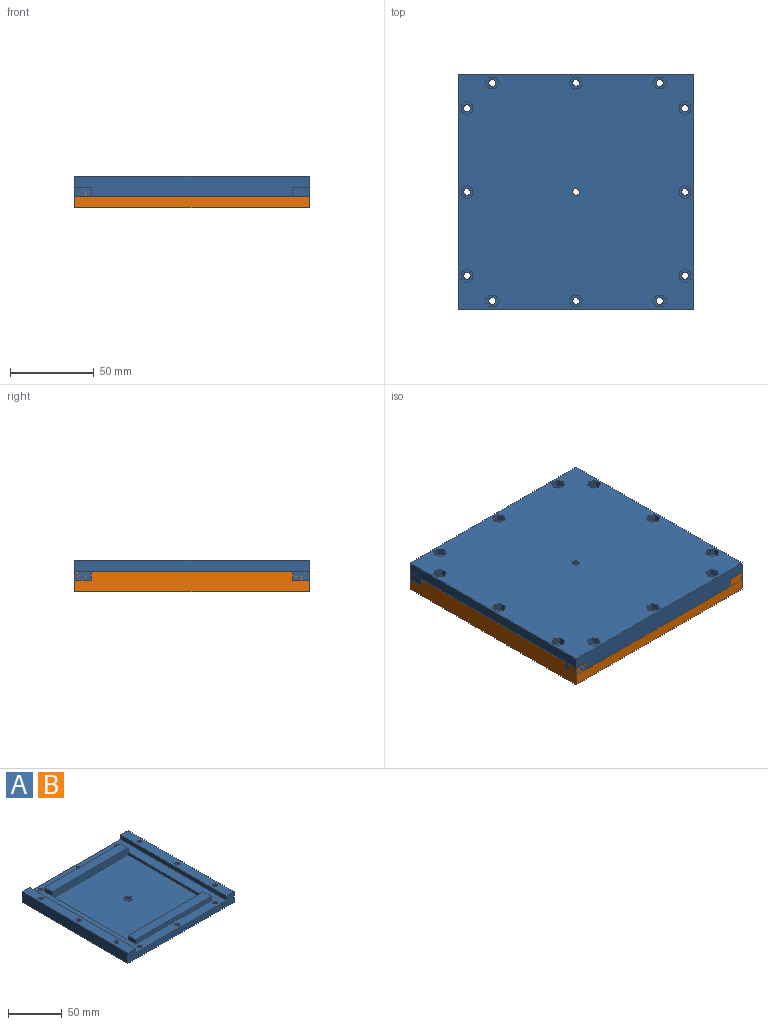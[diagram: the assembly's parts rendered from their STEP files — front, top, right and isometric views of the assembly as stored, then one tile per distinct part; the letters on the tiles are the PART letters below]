
ASSEMBLY  parts=2 mates=1
PART A: 127 faces, bbox 140x140x12 mm
  f0: plane 140x140mm, normal (0,0,-1), area 19062.3mm2, adj f15,f16,f17,f18,f42,f43,f44,f45
  f1: cylinder r=2.1mm len=8mm, axis (0,0,1), area 105.6mm2, adj f34,f126
  f2: cylinder r=2.1mm len=8mm, axis (0,0,1), area 105.6mm2, adj f34,f119
  f3: cylinder r=2.1mm len=8mm, axis (0,0,1), area 105.6mm2, adj f34,f112
  f4: cylinder r=2.1mm len=8mm, axis (0,0,1), area 105.6mm2, adj f32,f105
  f5: cylinder r=2.1mm len=8mm, axis (0,0,1), area 105.6mm2, adj f32,f98
  f6: cylinder r=2.1mm len=8mm, axis (0,0,1), area 105.6mm2, adj f32,f91
  f7: cylinder r=2.1mm len=4.2mm, axis (0,0,1), area 39.6mm2, adj f14,f84
  f8: cylinder r=2.1mm len=4.2mm, axis (0,0,1), area 39.6mm2, adj f14,f77
  f9: cylinder r=2.1mm len=4.2mm, axis (0,0,1), area 39.6mm2, adj f14,f70
  f10: cylinder r=2.1mm len=4.2mm, axis (0,0,1), area 39.6mm2, adj f14,f63
  f11: cylinder r=2.1mm len=4.2mm, axis (0,0,1), area 39.6mm2, adj f14,f56
  f12: cylinder r=2.1mm len=4.2mm, axis (0,0,1), area 39.6mm2, adj f14,f49
  f13: plane 100x100mm, normal (0,0,1), area 9956.3mm2, adj f19,f20,f21,f22,f35,f36,f37,f38
  f14: plane 140x120mm, normal (0,0,1), area 4716.9mm2, adj f7,f8,f9,f10,f11,f12,f16,f18
  f15: plane 140x12mm, normal (1,0,0), area 1680mm2, adj f0,f16,f18,f32
  f16: plane 140x12mm, normal (0,1,0), area 1080mm2, adj f0,f14,f15,f17,f31,f32,f33,f34
  f17: plane 140x12mm, normal (-1,0,0), area 1680mm2, adj f0,f16,f18,f34
  f18: plane 140x12mm, normal (0,-1,0), area 1080mm2, adj f0,f14,f15,f17,f31,f32,f33,f34
  f19: plane 100x8mm, normal (0,-1,0), area 800mm2, adj f13,f20,f22,f23,f24,f26
  f20: plane 100x3mm, normal (-1,0,0), area 300mm2, adj f13,f14,f19,f21
  f21: plane 100x8mm, normal (0,1,0), area 800mm2, adj f13,f20,f22,f27,f29,f30
  f22: plane 100x3mm, normal (1,0,0), area 300mm2, adj f13,f14,f19,f21
  f23: plane 10x5mm, normal (-1,0,0), area 50mm2, adj f14,f19,f25,f26
  f24: plane 10x5mm, normal (1,0,0), area 50mm2, adj f14,f19,f25,f26
  f25: plane 100x5mm, normal (0,1,0), area 500mm2, adj f14,f23,f24,f26
  f26: plane 100x10mm, normal (0,0,1), area 1000mm2, adj f19,f23,f24,f25
  f27: plane 10x5mm, normal (-1,0,0), area 50mm2, adj f14,f21,f28,f30
  f28: plane 100x5mm, normal (0,-1,0), area 500mm2, adj f14,f27,f29,f30
  f29: plane 10x5mm, normal (1,0,0), area 50mm2, adj f14,f21,f28,f30
  f30: plane 100x10mm, normal (0,0,1), area 1000mm2, adj f21,f27,f28,f29
  f31: plane 140x5mm, normal (-1,0,0), area 700mm2, adj f14,f16,f18,f32
  f32: plane 140x10mm, normal (0,0,1), area 1358.4mm2, adj f4,f5,f6,f15,f16,f18,f31
  f33: plane 140x5mm, normal (1,0,0), area 700mm2, adj f14,f16,f18,f34
  f34: plane 140x10mm, normal (0,0,1), area 1358.4mm2, adj f1,f2,f3,f16,f17,f18,f33
  f35: plane 3.55x3mm, normal (-0.87,0.5,0), area 12.3mm2, adj f13,f36,f40,f41
  f36: plane 3.55x3mm, normal (-0.87,-0.5,0), area 12.3mm2, adj f13,f35,f37,f41
  f37: plane 4.1x3mm, normal (0,-1,0), area 12.3mm2, adj f13,f36,f38,f41
  f38: plane 3.55x3mm, normal (0.87,-0.5,0), area 12.3mm2, adj f13,f37,f39,f41
  f39: plane 3.55x3mm, normal (0.87,0.5,0), area 12.3mm2, adj f13,f38,f40,f41
  f40: plane 4.1x3mm, normal (0,1,0), area 12.3mm2, adj f13,f35,f39,f41
  f41: plane 8.2x7.1mm, normal (0,0,1), area 29.8mm2, adj f35,f36,f37,f38,f39,f40,f42
  f42: cylinder r=2.1mm len=4.2mm, axis (0,0,1), area 13.2mm2, adj f0,f41
  f43: plane 4x3.55mm, normal (-0.87,0.5,0), area 16.4mm2, adj f0,f44,f48,f49
  f44: plane 4.1x4mm, normal (0,1,0), area 16.4mm2, adj f0,f43,f45,f49
  f45: plane 4x3.55mm, normal (0.87,0.5,0), area 16.4mm2, adj f0,f44,f46,f49
  f46: plane 4x3.55mm, normal (0.87,-0.5,0), area 16.4mm2, adj f0,f45,f47,f49
  f47: plane 4.1x4mm, normal (0,-1,0), area 16.4mm2, adj f0,f46,f48,f49
  f48: plane 4x3.55mm, normal (-0.87,-0.5,0), area 16.4mm2, adj f0,f43,f47,f49
  f49: plane 8.2x7.1mm, normal (0,0,-1), area 29.8mm2, adj f12,f43,f44,f45,f46,f47,f48
  f50: plane 4x3.55mm, normal (-0.87,0.5,0), area 16.4mm2, adj f0,f51,f55,f56
  f51: plane 4.1x4mm, normal (0,1,0), area 16.4mm2, adj f0,f50,f52,f56
  f52: plane 4x3.55mm, normal (0.87,0.5,0), area 16.4mm2, adj f0,f51,f53,f56
  f53: plane 4x3.55mm, normal (0.87,-0.5,0), area 16.4mm2, adj f0,f52,f54,f56
  f54: plane 4.1x4mm, normal (0,-1,0), area 16.4mm2, adj f0,f53,f55,f56
  f55: plane 4x3.55mm, normal (-0.87,-0.5,0), area 16.4mm2, adj f0,f50,f54,f56
  f56: plane 8.2x7.1mm, normal (0,0,-1), area 29.8mm2, adj f11,f50,f51,f52,f53,f54,f55
  f57: plane 4x3.55mm, normal (0.87,-0.5,0), area 16.4mm2, adj f0,f58,f62,f63
  f58: plane 4.1x4mm, normal (0,-1,0), area 16.4mm2, adj f0,f57,f59,f63
  f59: plane 4x3.55mm, normal (-0.87,-0.5,0), area 16.4mm2, adj f0,f58,f60,f63
  f60: plane 4x3.55mm, normal (-0.87,0.5,0), area 16.4mm2, adj f0,f59,f61,f63
  f61: plane 4.1x4mm, normal (0,1,0), area 16.4mm2, adj f0,f60,f62,f63
  f62: plane 4x3.55mm, normal (0.87,0.5,0), area 16.4mm2, adj f0,f57,f61,f63
  f63: plane 8.2x7.1mm, normal (0,0,-1), area 29.8mm2, adj f10,f57,f58,f59,f60,f61,f62
  f64: plane 4x3.55mm, normal (-0.87,-0.5,0), area 16.4mm2, adj f0,f65,f69,f70
  f65: plane 4x3.55mm, normal (-0.87,0.5,0), area 16.4mm2, adj f0,f64,f66,f70
  f66: plane 4.1x4mm, normal (0,1,0), area 16.4mm2, adj f0,f65,f67,f70
  f67: plane 4x3.55mm, normal (0.87,0.5,0), area 16.4mm2, adj f0,f66,f68,f70
  f68: plane 4x3.55mm, normal (0.87,-0.5,0), area 16.4mm2, adj f0,f67,f69,f70
  f69: plane 4.1x4mm, normal (0,-1,0), area 16.4mm2, adj f0,f64,f68,f70
  f70: plane 8.2x7.1mm, normal (0,0,-1), area 29.8mm2, adj f9,f64,f65,f66,f67,f68,f69
  f71: plane 4x3.55mm, normal (-0.87,0.5,0), area 16.4mm2, adj f0,f72,f76,f77
  f72: plane 4.1x4mm, normal (0,1,0), area 16.4mm2, adj f0,f71,f73,f77
  f73: plane 4x3.55mm, normal (0.87,0.5,0), area 16.4mm2, adj f0,f72,f74,f77
  f74: plane 4x3.55mm, normal (0.87,-0.5,0), area 16.4mm2, adj f0,f73,f75,f77
  f75: plane 4.1x4mm, normal (0,-1,0), area 16.4mm2, adj f0,f74,f76,f77
  f76: plane 4x3.55mm, normal (-0.87,-0.5,0), area 16.4mm2, adj f0,f71,f75,f77
  f77: plane 8.2x7.1mm, normal (0,0,-1), area 29.8mm2, adj f8,f71,f72,f73,f74,f75,f76
  f78: plane 4x3.55mm, normal (0.87,0.5,0), area 16.4mm2, adj f0,f79,f83,f84
  f79: plane 4x3.55mm, normal (0.87,-0.5,0), area 16.4mm2, adj f0,f78,f80,f84
  f80: plane 4.1x4mm, normal (0,-1,0), area 16.4mm2, adj f0,f79,f81,f84
  f81: plane 4x3.55mm, normal (-0.87,-0.5,0), area 16.4mm2, adj f0,f80,f82,f84
  f82: plane 4x3.55mm, normal (-0.87,0.5,0), area 16.4mm2, adj f0,f81,f83,f84
  f83: plane 4.1x4mm, normal (0,1,0), area 16.4mm2, adj f0,f78,f82,f84
  f84: plane 8.2x7.1mm, normal (0,0,-1), area 29.8mm2, adj f7,f78,f79,f80,f81,f82,f83
  f85: plane 4x3.55mm, normal (0.5,-0.87,0), area 16.4mm2, adj f0,f86,f90,f91
  f86: plane 4x3.55mm, normal (-0.5,-0.87,0), area 16.4mm2, adj f0,f85,f87,f91
  f87: plane 4.1x4mm, normal (-1,0,0), area 16.4mm2, adj f0,f86,f88,f91
  f88: plane 4x3.55mm, normal (-0.5,0.87,0), area 16.4mm2, adj f0,f87,f89,f91
  f89: plane 4x3.55mm, normal (0.5,0.87,0), area 16.4mm2, adj f0,f88,f90,f91
  f90: plane 4.1x4mm, normal (1,0,0), area 16.4mm2, adj f0,f85,f89,f91
  f91: plane 8.2x7.1mm, normal (0,0,-1), area 29.8mm2, adj f6,f85,f86,f87,f88,f89,f90
  f92: plane 4x3.55mm, normal (0.5,0.87,0), area 16.4mm2, adj f0,f93,f97,f98
  f93: plane 4.1x4mm, normal (1,0,0), area 16.4mm2, adj f0,f92,f94,f98
  f94: plane 4x3.55mm, normal (0.5,-0.87,0), area 16.4mm2, adj f0,f93,f95,f98
  f95: plane 4x3.55mm, normal (-0.5,-0.87,0), area 16.4mm2, adj f0,f94,f96,f98
  f96: plane 4.1x4mm, normal (-1,0,0), area 16.4mm2, adj f0,f95,f97,f98
  f97: plane 4x3.55mm, normal (-0.5,0.87,0), area 16.4mm2, adj f0,f92,f96,f98
  f98: plane 8.2x7.1mm, normal (0,0,-1), area 29.8mm2, adj f5,f92,f93,f94,f95,f96,f97
  f99: plane 4x3.55mm, normal (0.5,0.87,0), area 16.4mm2, adj f0,f100,f104,f105
  f100: plane 4.1x4mm, normal (1,0,0), area 16.4mm2, adj f0,f99,f101,f105
  f101: plane 4x3.55mm, normal (0.5,-0.87,0), area 16.4mm2, adj f0,f100,f102,f105
  f102: plane 4x3.55mm, normal (-0.5,-0.87,0), area 16.4mm2, adj f0,f101,f103,f105
  f103: plane 4.1x4mm, normal (-1,0,0), area 16.4mm2, adj f0,f102,f104,f105
  f104: plane 4x3.55mm, normal (-0.5,0.87,0), area 16.4mm2, adj f0,f99,f103,f105
  f105: plane 8.2x7.1mm, normal (0,0,-1), area 29.8mm2, adj f4,f99,f100,f101,f102,f103,f104
  f106: plane 4x3.55mm, normal (-0.5,-0.87,0), area 16.4mm2, adj f0,f107,f111,f112
  f107: plane 4.1x4mm, normal (-1,0,0), area 16.4mm2, adj f0,f106,f108,f112
  f108: plane 4x3.55mm, normal (-0.5,0.87,0), area 16.4mm2, adj f0,f107,f109,f112
  f109: plane 4x3.55mm, normal (0.5,0.87,0), area 16.4mm2, adj f0,f108,f110,f112
  f110: plane 4.1x4mm, normal (1,0,0), area 16.4mm2, adj f0,f109,f111,f112
  f111: plane 4x3.55mm, normal (0.5,-0.87,0), area 16.4mm2, adj f0,f106,f110,f112
  f112: plane 8.2x7.1mm, normal (0,0,-1), area 29.8mm2, adj f3,f106,f107,f108,f109,f110,f111
  f113: plane 4x3.55mm, normal (-0.5,-0.87,0), area 16.4mm2, adj f0,f114,f118,f119
  f114: plane 4.1x4mm, normal (-1,0,0), area 16.4mm2, adj f0,f113,f115,f119
  f115: plane 4x3.55mm, normal (-0.5,0.87,0), area 16.4mm2, adj f0,f114,f116,f119
  f116: plane 4x3.55mm, normal (0.5,0.87,0), area 16.4mm2, adj f0,f115,f117,f119
  f117: plane 4.1x4mm, normal (1,0,0), area 16.4mm2, adj f0,f116,f118,f119
  f118: plane 4x3.55mm, normal (0.5,-0.87,0), area 16.4mm2, adj f0,f113,f117,f119
  f119: plane 8.2x7.1mm, normal (0,0,-1), area 29.8mm2, adj f2,f113,f114,f115,f116,f117,f118
  f120: plane 4x3.55mm, normal (-0.5,-0.87,0), area 16.4mm2, adj f0,f121,f125,f126
  f121: plane 4.1x4mm, normal (-1,0,0), area 16.4mm2, adj f0,f120,f122,f126
  f122: plane 4x3.55mm, normal (-0.5,0.87,0), area 16.4mm2, adj f0,f121,f123,f126
  f123: plane 4x3.55mm, normal (0.5,0.87,0), area 16.4mm2, adj f0,f122,f124,f126
  f124: plane 4.1x4mm, normal (1,0,0), area 16.4mm2, adj f0,f123,f125,f126
  f125: plane 4x3.55mm, normal (0.5,-0.87,0), area 16.4mm2, adj f0,f120,f124,f126
  f126: plane 8.2x7.1mm, normal (0,0,-1), area 29.8mm2, adj f1,f120,f121,f122,f123,f124,f125
PART B: same geometry as A
PLACE A rot(axis=(0.71,0.71,0),180deg) t=(2.29,0.7,12.07)mm
PLACE B t=(2.29,0.7,-6.93)mm fixed
MATE fastened A.f30 <-> B.f14  axis (0,0,-1) through (-57.71,0.7,0.07)mm
